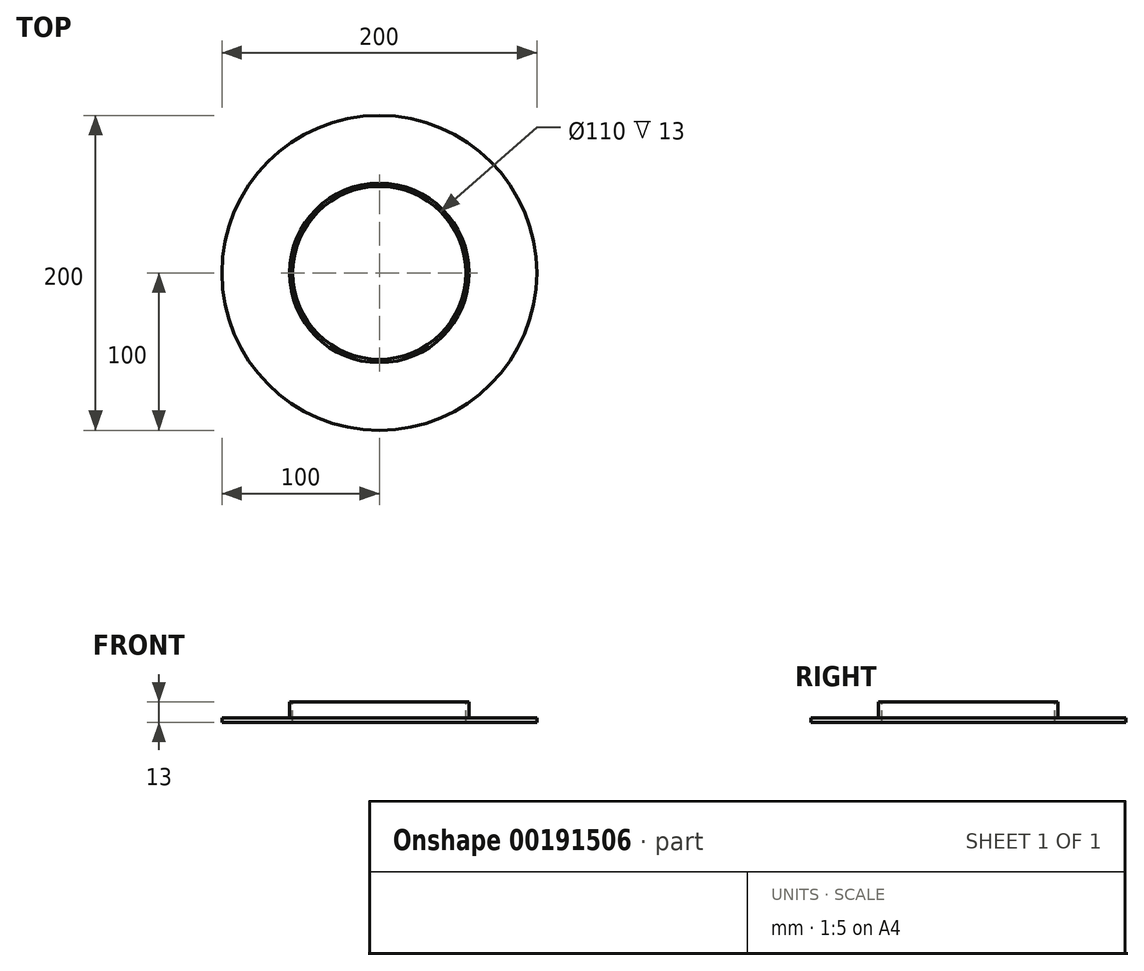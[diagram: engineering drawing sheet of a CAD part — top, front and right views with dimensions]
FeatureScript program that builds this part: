
annotation { "Feature Type Name" : "Feature", "Feature Type Description" : "" }
export const myFeature = defineFeature(function(context is Context, id is Id, definition is map)
    precondition{}
    {
        {
            var Q0;
            Q0=qCreatedBy(makeId("Top.planeOp"),FACE);
            var sketch = newSketch(context, id + "F0", { "sketchPlane" : qUnion([Q0])});
            skCircle(sketch, "E0", {"center": v(0, 0) * mm, "radius": 100 * mm});
            skSolve(sketch);
        }
        {
            var Q0;
            Q0 = qSketchRegion(id + "F0", true);
            extrude(context, id + "F1", {"entities" : qUnion([Q0]), "depth" : 3 * mm});
        }
        {
            var Q0;
            Q0=makeQuery(id+"F1.opExtrude","CAP_FACE",FACE,{"disambiguationData":[OSD([sQuery(id+"F0.wireOp",EDGE,"E0")])],"isStart":false});
            var sketch = newSketch(context, id + "F2", { "sketchPlane" : qUnion([Q0])});
            skCircle(sketch, "E1", {"center": v(0, 0) * mm, "radius": 55 * mm});
            skSolve(sketch);
        }
        {
            var Q0;
            Q0 = qSketchRegion(id + "F2", true);
            extrude(context, id + "F3", {"entities" : qUnion([Q0]), "operationType" : NewBodyOperationType.REMOVE, "oppositeDirection" : true, "depth" : 25 * mm});
        }
        {
            var Q0;
            Q0=makeQuery(id+"F1.opExtrude","CAP_FACE",FACE,{"disambiguationData":[OSD([sQuery(id+"F0.wireOp",EDGE,"E0")])],"isStart":false});
            var sketch = newSketch(context, id + "F4", { "sketchPlane" : qUnion([Q0])});
            skCircle(sketch, "E2", {"center": v(0, 0) * mm, "radius": 55 * mm});
            skCircle(sketch, "E3", {"center": v(0, 0) * mm, "radius": 57 * mm});
            skSolve(sketch);
        }
        {
            var Q0;
            Q0=makeQuery(id+"F4.imprint","IMPRINT",FACE,{"disambiguationData":[TD([[makeQuery(id+"F4.imprint","IMPRINT",EDGE,{"derivedFrom":sQuery(id+"F4.wireOp",EDGE,"E2")}),-1.0]])]});
            extrude(context, id + "F5", {"entities" : qUnion([Q0]), "operationType" : NewBodyOperationType.ADD, "depth" : 10 * mm});
        }
    });
